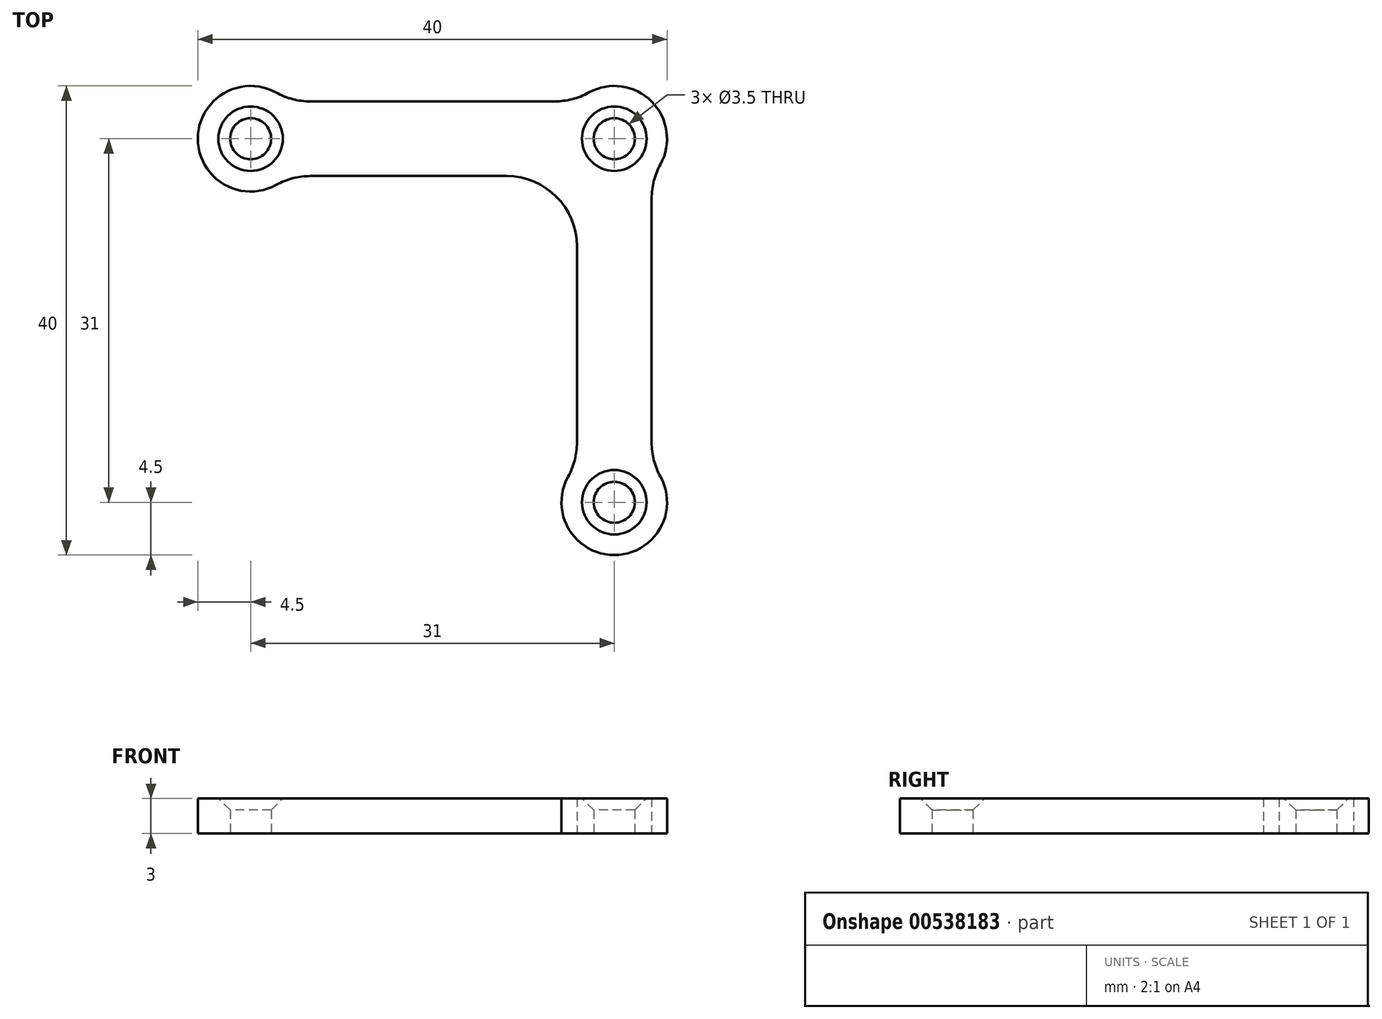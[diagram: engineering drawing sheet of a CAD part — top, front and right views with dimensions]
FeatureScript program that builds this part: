
annotation { "Feature Type Name" : "Feature", "Feature Type Description" : "" }
export const myFeature = defineFeature(function(context is Context, id is Id, definition is map)
    precondition{}
    {
        {
            var Q0;
            Q0=qCreatedBy(makeId("Top.planeOp"),FACE);
            var sketch = newSketch(context, id + "F0", { "sketchPlane" : qUnion([Q0])});
            skLineSegment(sketch, "E0.bottom", {"start": v(-15.5, 15.5) * mm, "end": v(15.5, 15.5) * mm, "construction": true});
            skLineSegment(sketch, "E0.top", {"start": v(-15.5, -15.5) * mm, "end": v(15.5, -15.5) * mm, "construction": true});
            skLineSegment(sketch, "E0.left", {"start": v(-15.5, 15.5) * mm, "end": v(-15.5, -15.5) * mm, "construction": true});
            skLineSegment(sketch, "E0.right", {"start": v(15.5, 15.5) * mm, "end": v(15.5, -15.5) * mm, "construction": true});
            skCircle(sketch, "E1", {"center": v(-15.5, 15.5) * mm, "radius": 1.75 * mm});
            skCircle(sketch, "E2", {"center": v(15.5, 15.5) * mm, "radius": 1.75 * mm});
            skCircle(sketch, "E3", {"center": v(15.5, -15.5) * mm, "radius": 1.75 * mm});
            skCircle(sketch, "E4", {"center": v(15.5, 15.5) * mm, "radius": 4.5 * mm, "construction": true});
            skCircle(sketch, "E5", {"center": v(15.5, -15.5) * mm, "radius": 4.5 * mm, "construction": true});
            skLineSegment(sketch, "E6.bottom", {"start": v(-10.4, 18.68) * mm, "end": v(10.4, 18.68) * mm});
            skLineSegment(sketch, "E6.top", {"start": v(-10.4, 12.32) * mm, "end": v(6.32, 12.32) * mm});
            skLineSegment(sketch, "E6.left", {"start": v(-12.32, 18.68) * mm, "end": v(-12.32, 18.68) * mm});
            skLineSegment(sketch, "E6.right", {"start": v(12.32, 18.68) * mm, "end": v(12.32, 12.32) * mm, "construction": true});
            skLineSegment(sketch, "E7.bottom", {"start": v(12.32, 12.32) * mm, "end": v(18.68, 12.32) * mm, "construction": true});
            skLineSegment(sketch, "E7.top", {"start": v(12.32, -12.32) * mm, "end": v(18.68, -12.32) * mm, "construction": true});
            skLineSegment(sketch, "E7.left", {"start": v(12.32, 12.32) * mm, "end": v(12.32, 12.32) * mm});
            skLineSegment(sketch, "E7.right", {"start": v(18.68, 10.4) * mm, "end": v(18.68, -10.4) * mm});
            skLineSegment(sketch, "E8", {"start": v(-12.32, 18.68) * mm, "end": v(-12.32, 12.32) * mm, "construction": true});
            skArc(sketch, "E9", {"start": v(-12.32, 12.32) * mm, "mid": v(-11, 15.5) * mm, "end": v(-12.32, 18.68) * mm, "construction": true});
            skArc(sketch, "E10", {"start": v(-13.32, 19.44) * mm, "mid": v(-20, 15.5) * mm, "end": v(-13.32, 11.56) * mm});
            skLineSegment(sketch, "E11", {"start": v(12.32, 6.32) * mm, "end": v(12.32, -10.4) * mm});
            skArc(sketch, "E12", {"start": v(19.44, 13.32) * mm, "mid": v(18.68, 18.68) * mm, "end": v(13.32, 19.44) * mm});
            skArc(sketch, "E13", {"start": v(11.56, -13.32) * mm, "mid": v(15.5, -20) * mm, "end": v(19.44, -13.32) * mm});
            skPoint(sketch, "E14.visualSharp", {"position": v(12.32, 12.32) * mm});
            skArc(sketch, "E14.filletArc", {"start": v(12.32, 6.32) * mm, "mid": v(10.56, 10.56) * mm, "end": v(6.32, 12.32) * mm});
            skPoint(sketch, "E15.visualSharp", {"position": v(12.32, 18.68) * mm});
            skArc(sketch, "E15.filletArc", {"start": v(10.4, 18.68) * mm, "mid": v(11.9, 18.87) * mm, "end": v(13.32, 19.44) * mm});
            skPoint(sketch, "E16.visualSharp", {"position": v(18.68, 12.32) * mm});
            skArc(sketch, "E16.filletArc", {"start": v(19.44, 13.32) * mm, "mid": v(18.87, 11.9) * mm, "end": v(18.68, 10.4) * mm});
            skPoint(sketch, "E17.visualSharp", {"position": v(-12.32, 18.68) * mm});
            skArc(sketch, "E17.filletArc", {"start": v(-13.32, 19.44) * mm, "mid": v(-11.9, 18.87) * mm, "end": v(-10.4, 18.68) * mm});
            skPoint(sketch, "E18.visualSharp", {"position": v(-12.32, 12.32) * mm});
            skArc(sketch, "E18.filletArc", {"start": v(-10.4, 12.32) * mm, "mid": v(-11.9, 12.13) * mm, "end": v(-13.32, 11.56) * mm});
            skPoint(sketch, "E19.visualSharp", {"position": v(12.32, -12.32) * mm});
            skArc(sketch, "E19.filletArc", {"start": v(11.56, -13.32) * mm, "mid": v(12.13, -11.9) * mm, "end": v(12.32, -10.4) * mm});
            skPoint(sketch, "E20.visualSharp", {"position": v(18.68, -12.32) * mm});
            skArc(sketch, "E20.filletArc", {"start": v(18.68, -10.4) * mm, "mid": v(18.87, -11.9) * mm, "end": v(19.44, -13.32) * mm});
            skSolve(sketch);
        }
        {
            var Q0;
            Q0=makeQuery(id+"F0.imprint","IMPRINT",FACE,{"disambiguationData":[TD([[makeQuery(id+"F0.imprint","IMPRINT",EDGE,{"derivedFrom":sQuery(id+"F0.wireOp",EDGE,"E1")}),-1.0]])]});
            extrude(context, id + "F1", {"entities" : qUnion([Q0]), "depth" : 3 * mm, "offsetDistance" : 25.4 * mm});
        }
        {
            var Q0;
            Q0=makeQuery(id+"F1.opExtrude","CAP_EDGE",EDGE,{"disambiguationData":[OSD([sQuery(id+"F0.wireOp",EDGE,"E1")])],"isStart":false});
            var Q1;
            Q1=makeQuery(id+"F1.opExtrude","CAP_EDGE",EDGE,{"disambiguationData":[OSD([sQuery(id+"F0.wireOp",EDGE,"E2")])],"isStart":false});
            var Q2;
            Q2=makeQuery(id+"F1.opExtrude","CAP_EDGE",EDGE,{"disambiguationData":[OSD([sQuery(id+"F0.wireOp",EDGE,"E3")])],"isStart":false});
            chamfer(context, id + "F2", {"entities" : qUnion([Q0, Q1, Q2]), "width" : 1 * mm, "tangentPropagation" : true});
        }
    });
